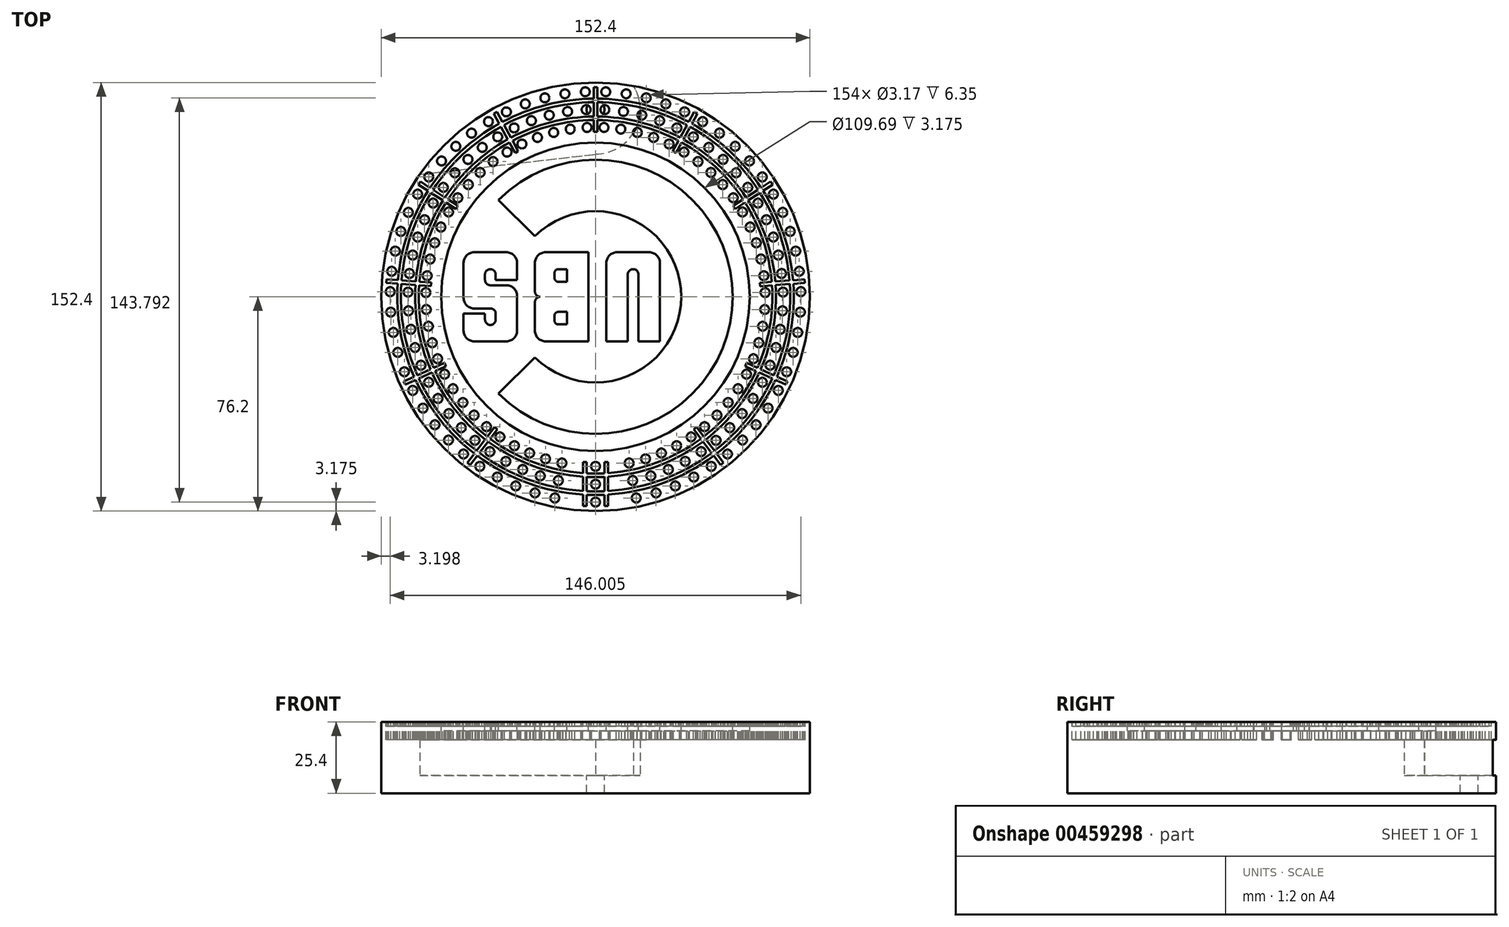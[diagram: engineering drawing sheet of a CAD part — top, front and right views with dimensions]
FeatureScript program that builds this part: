
annotation { "Feature Type Name" : "Feature", "Feature Type Description" : "" }
export const myFeature = defineFeature(function(context is Context, id is Id, definition is map)
    precondition{}
    {
        {
            var Q0;
            Q0=qCreatedBy(makeId("Top.planeOp"),FACE);
            var sketch = newSketch(context, id + "F0", { "sketchPlane" : qUnion([Q0])});
            skCircle(sketch, "E0", {"center": v(0, 0) * mm, "radius": 76.2 * mm});
            skSolve(sketch);
        }
        {
            var Q0;
            Q0=makeQuery(id+"F0.imprint","IMPRINT",FACE,{"disambiguationData":[TD([[makeQuery(id+"F0.imprint","IMPRINT",EDGE,{"derivedFrom":sQuery(id+"F0.wireOp",EDGE,"E0")}),1.0]])]});
            extrude(context, id + "F1", {"entities" : qUnion([Q0]), "depth" : 6.35 * mm});
        }
        {
            var Q0;
            Q0=makeQuery(id+"F1.opExtrude","CAP_FACE",FACE,{"disambiguationData":[OSD([sQuery(id+"F0.wireOp",EDGE,"E0")])],"isStart":false});
            var sketch = newSketch(context, id + "F2", { "sketchPlane" : qUnion([Q0])});
            skCircle(sketch, "E1", {"center": v(0, 66.68) * mm, "radius": 3.18 * mm});
            skSolve(sketch);
        }
        {
            var Q0;
            Q0 = qSketchRegion(id + "F2", true);
            extrude(context, id + "F3", {"entities" : qUnion([Q0]), "operationType" : NewBodyOperationType.REMOVE, "oppositeDirection" : true, "depth" : 6.35 * mm});
        }
        {
            var Q0;
            Q0=makeQuery(id+"F1.opExtrude","CAP_FACE",FACE,{"disambiguationData":[OSD([sQuery(id+"F0.wireOp",EDGE,"E0")])],"isStart":false});
            var sketch = newSketch(context, id + "F4", { "sketchPlane" : qUnion([Q0])});
            skArc(sketch, "E2", {"start": v(0, 50.8) * mm, "mid": v(13.86, 58.93) * mm, "end": v(13.52, 75) * mm});
            skLineSegment(sketch, "E3", {"start": v(-62.53, 43.54) * mm, "end": v(0, 50.7) * mm});
            skLineSegment(sketch, "E4", {"start": v(0, 50.7) * mm, "end": v(0, 50.8) * mm});
            skSolve(sketch);
        }
        {
            var Q0;
            {var subQ0=sQuery(id+"F4.wireOp",EDGE,"E2");Q0=makeQuery(id+"F4.imprint","IMPRINT",FACE,{"disambiguationData":[TD([[makeQuery(id+"F4.imprint","IMPRINT",EDGE,{"derivedFrom":subQ0}),-1.0]])]});}
            extrude(context, id + "F5", {"entities" : qUnion([Q0]), "operationType" : NewBodyOperationType.ADD, "depth" : 12.7 * mm});
        }
        {
            var Q0;
            Q0=makeQuery(id+"F5.opExtrude","CAP_FACE",FACE,{"disambiguationData":[OSD([sQuery(id+"F0.wireOp",EDGE,"E0"),sQuery(id+"F4.wireOp",EDGE,"E2"),sQuery(id+"F4.wireOp",EDGE,"E3"),sQuery(id+"F4.wireOp",EDGE,"E4")])],"isStart":false});
            var sketch = newSketch(context, id + "F6", { "sketchPlane" : qUnion([Q0])});
            skCircle(sketch, "E5", {"center": v(0, 0) * mm, "radius": 76.2 * mm});
            skSolve(sketch);
        }
        {
            var Q0;
            {var subQ1=makeQuery(id+"F5.opExtrude","CAP_EDGE",EDGE,{"disambiguationData":[OSD([sQuery(id+"F4.wireOp",EDGE,"E2")])],"isStart":false});Q0=makeQuery(id+"F6.imprint","IMPRINT",FACE,{"disambiguationData":[TD([[makeQuery(id+"F6.imprint","IMPRINT",EDGE,{"derivedFrom":subQ1}),-1.0]])]});}
            var Q1;
            {var subQ1=makeQuery(id+"F5.opExtrude","CAP_EDGE",EDGE,{"disambiguationData":[OSD([sQuery(id+"F4.wireOp",EDGE,"E2")])],"isStart":false});Q1=makeQuery(id+"F6.imprint","IMPRINT",FACE,{"disambiguationData":[TD([[makeQuery(id+"F6.imprint","IMPRINT",EDGE,{"derivedFrom":subQ1}),1.0]])]});}
            extrude(context, id + "F7", {"entities" : qUnion([Q0, Q1]), "operationType" : NewBodyOperationType.ADD, "depth" : 6.35 * mm});
        }
        {
            var Q0;
            Q0=makeQuery(id+"F7.opExtrude","CAP_FACE",FACE,{"disambiguationData":[OSD([sQuery(id+"F6.wireOp",EDGE,"E5")])],"isStart":false});
            var sketch = newSketch(context, id + "F8", { "sketchPlane" : qUnion([Q0])});
            skCircle(sketch, "E6", {"center": v(0, -73.03) * mm, "radius": 1.59 * mm});
            skCircle(sketch, "E7.1.0", {"center": v(7.27, -72.66) * mm, "radius": 1.59 * mm});
            skCircle(sketch, "E7.2.0", {"center": v(14.47, -71.58) * mm, "radius": 1.59 * mm});
            skCircle(sketch, "E7.3.0", {"center": v(21.52, -69.78) * mm, "radius": 1.59 * mm});
            skCircle(sketch, "E7.4.0", {"center": v(28.37, -67.3) * mm, "radius": 1.59 * mm});
            skCircle(sketch, "E7.5.0", {"center": v(34.92, -64.13) * mm, "radius": 1.59 * mm});
            skCircle(sketch, "E7.6.0", {"center": v(41.14, -60.34) * mm, "radius": 1.59 * mm});
            skCircle(sketch, "E7.7.0", {"center": v(46.94, -55.94) * mm, "radius": 1.59 * mm});
            skCircle(sketch, "E7.8.0", {"center": v(52.28, -50.99) * mm, "radius": 1.59 * mm});
            skCircle(sketch, "E7.9.0", {"center": v(57.1, -45.53) * mm, "radius": 1.59 * mm});
            skCircle(sketch, "E7.10.0", {"center": v(61.34, -39.62) * mm, "radius": 1.59 * mm});
            skCircle(sketch, "E7.11.0", {"center": v(64.98, -33.31) * mm, "radius": 1.59 * mm});
            skCircle(sketch, "E7.12.0", {"center": v(67.98, -26.68) * mm, "radius": 1.59 * mm});
            skCircle(sketch, "E7.13.0", {"center": v(70.3, -19.78) * mm, "radius": 1.59 * mm});
            skCircle(sketch, "E7.14.0", {"center": v(71.92, -12.68) * mm, "radius": 1.59 * mm});
            skCircle(sketch, "E7.15.0", {"center": v(72.82, -5.46) * mm, "radius": 1.59 * mm});
            skCircle(sketch, "E7.16.0", {"center": v(73, 1.82) * mm, "radius": 1.59 * mm});
            skCircle(sketch, "E7.17.0", {"center": v(72.46, 9.08) * mm, "radius": 1.59 * mm});
            skCircle(sketch, "E7.18.0", {"center": v(71.2, 16.25) * mm, "radius": 1.59 * mm});
            skCircle(sketch, "E7.19.0", {"center": v(69.22, 23.26) * mm, "radius": 1.59 * mm});
            skCircle(sketch, "E7.20.0", {"center": v(66.56, 30.03) * mm, "radius": 1.59 * mm});
            skCircle(sketch, "E7.21.0", {"center": v(63.24, 36.51) * mm, "radius": 1.59 * mm});
            skCircle(sketch, "E7.22.0", {"center": v(59.3, 42.63) * mm, "radius": 1.59 * mm});
            skCircle(sketch, "E7.23.0", {"center": v(54.75, 48.32) * mm, "radius": 1.59 * mm});
            skCircle(sketch, "E7.24.0", {"center": v(49.67, 53.53) * mm, "radius": 1.59 * mm});
            skCircle(sketch, "E7.25.0", {"center": v(44.1, 58.21) * mm, "radius": 1.59 * mm});
            skCircle(sketch, "E7.26.0", {"center": v(38.08, 62.31) * mm, "radius": 1.59 * mm});
            skCircle(sketch, "E7.27.0", {"center": v(31.68, 65.8) * mm, "radius": 1.59 * mm});
            skCircle(sketch, "E7.28.0", {"center": v(24.98, 68.62) * mm, "radius": 1.59 * mm});
            skCircle(sketch, "E7.29.0", {"center": v(18.02, 70.77) * mm, "radius": 1.59 * mm});
            skCircle(sketch, "E7.30.0", {"center": v(10.88, 72.2) * mm, "radius": 1.59 * mm});
            skCircle(sketch, "E7.31.0", {"center": v(3.64, 72.93) * mm, "radius": 1.59 * mm});
            skCircle(sketch, "E7.32.0", {"center": v(-3.64, 72.93) * mm, "radius": 1.59 * mm});
            skCircle(sketch, "E7.33.0", {"center": v(-10.88, 72.2) * mm, "radius": 1.59 * mm});
            skCircle(sketch, "E7.34.0", {"center": v(-18.02, 70.77) * mm, "radius": 1.59 * mm});
            skCircle(sketch, "E7.35.0", {"center": v(-24.98, 68.62) * mm, "radius": 1.59 * mm});
            skCircle(sketch, "E7.36.0", {"center": v(-31.68, 65.8) * mm, "radius": 1.59 * mm});
            skCircle(sketch, "E7.37.0", {"center": v(-38.08, 62.31) * mm, "radius": 1.59 * mm});
            skCircle(sketch, "E7.38.0", {"center": v(-44.1, 58.21) * mm, "radius": 1.59 * mm});
            skCircle(sketch, "E7.39.0", {"center": v(-49.67, 53.53) * mm, "radius": 1.59 * mm});
            skCircle(sketch, "E7.40.0", {"center": v(-54.75, 48.32) * mm, "radius": 1.59 * mm});
            skCircle(sketch, "E7.41.0", {"center": v(-59.3, 42.63) * mm, "radius": 1.59 * mm});
            skCircle(sketch, "E7.42.0", {"center": v(-63.24, 36.51) * mm, "radius": 1.59 * mm});
            skCircle(sketch, "E7.43.0", {"center": v(-66.56, 30.03) * mm, "radius": 1.59 * mm});
            skCircle(sketch, "E7.44.0", {"center": v(-69.22, 23.26) * mm, "radius": 1.59 * mm});
            skCircle(sketch, "E7.45.0", {"center": v(-71.2, 16.25) * mm, "radius": 1.59 * mm});
            skCircle(sketch, "E7.46.0", {"center": v(-72.46, 9.08) * mm, "radius": 1.59 * mm});
            skCircle(sketch, "E7.47.0", {"center": v(-73, 1.82) * mm, "radius": 1.59 * mm});
            skCircle(sketch, "E7.48.0", {"center": v(-72.82, -5.46) * mm, "radius": 1.59 * mm});
            skCircle(sketch, "E7.49.0", {"center": v(-71.92, -12.68) * mm, "radius": 1.59 * mm});
            skCircle(sketch, "E7.50.0", {"center": v(-70.3, -19.78) * mm, "radius": 1.59 * mm});
            skCircle(sketch, "E7.51.0", {"center": v(-67.98, -26.68) * mm, "radius": 1.59 * mm});
            skCircle(sketch, "E7.52.0", {"center": v(-64.98, -33.31) * mm, "radius": 1.59 * mm});
            skCircle(sketch, "E7.53.0", {"center": v(-61.34, -39.62) * mm, "radius": 1.59 * mm});
            skCircle(sketch, "E7.54.0", {"center": v(-57.1, -45.53) * mm, "radius": 1.59 * mm});
            skCircle(sketch, "E7.55.0", {"center": v(-52.28, -50.99) * mm, "radius": 1.59 * mm});
            skCircle(sketch, "E7.56.0", {"center": v(-46.94, -55.94) * mm, "radius": 1.59 * mm});
            skCircle(sketch, "E7.57.0", {"center": v(-41.14, -60.34) * mm, "radius": 1.59 * mm});
            skCircle(sketch, "E7.58.0", {"center": v(-34.92, -64.13) * mm, "radius": 1.59 * mm});
            skCircle(sketch, "E7.59.0", {"center": v(-28.37, -67.3) * mm, "radius": 1.59 * mm});
            skCircle(sketch, "E7.60.0", {"center": v(-21.52, -69.78) * mm, "radius": 1.59 * mm});
            skCircle(sketch, "E7.61.0", {"center": v(-14.47, -71.58) * mm, "radius": 1.59 * mm});
            skCircle(sketch, "E7.62.0", {"center": v(-7.27, -72.66) * mm, "radius": 1.59 * mm});
            skPoint(sketch, "E7.center", {"position": v(0, 0) * mm});
            skSolve(sketch);
        }
        {
            var Q0;
            Q0=makeQuery(id+"F8.imprint","IMPRINT",FACE,{"disambiguationData":[TD([[makeQuery(id+"F8.imprint","IMPRINT",EDGE,{"derivedFrom":sQuery(id+"F8.wireOp",EDGE,"E6")}),-1.0]])]});
            var sketch = newSketch(context, id + "F9", { "sketchPlane" : qUnion([Q0])});
            skCircle(sketch, "E8", {"center": v(0, -66.67) * mm, "radius": 1.59 * mm});
            skCircle(sketch, "E9.1.0", {"center": v(6.64, -66.34) * mm, "radius": 1.59 * mm});
            skCircle(sketch, "E9.2.0", {"center": v(13.21, -65.35) * mm, "radius": 1.59 * mm});
            skCircle(sketch, "E9.3.0", {"center": v(19.65, -63.71) * mm, "radius": 1.59 * mm});
            skCircle(sketch, "E9.4.0", {"center": v(25.9, -61.44) * mm, "radius": 1.59 * mm});
            skCircle(sketch, "E9.5.0", {"center": v(31.89, -58.56) * mm, "radius": 1.59 * mm});
            skCircle(sketch, "E9.6.0", {"center": v(37.56, -55.09) * mm, "radius": 1.59 * mm});
            skCircle(sketch, "E9.7.0", {"center": v(42.86, -51.08) * mm, "radius": 1.59 * mm});
            skCircle(sketch, "E9.8.0", {"center": v(47.73, -46.55) * mm, "radius": 1.59 * mm});
            skCircle(sketch, "E9.9.0", {"center": v(52.13, -41.57) * mm, "radius": 1.59 * mm});
            skCircle(sketch, "E9.10.0", {"center": v(56, -36.17) * mm, "radius": 1.59 * mm});
            skCircle(sketch, "E9.11.0", {"center": v(59.33, -30.42) * mm, "radius": 1.59 * mm});
            skCircle(sketch, "E9.12.0", {"center": v(62.07, -24.36) * mm, "radius": 1.59 * mm});
            skCircle(sketch, "E9.13.0", {"center": v(64.18, -18.06) * mm, "radius": 1.59 * mm});
            skCircle(sketch, "E9.14.0", {"center": v(65.66, -11.58) * mm, "radius": 1.59 * mm});
            skCircle(sketch, "E9.15.0", {"center": v(66.49, -4.98) * mm, "radius": 1.59 * mm});
            skCircle(sketch, "E9.16.0", {"center": v(66.65, 1.66) * mm, "radius": 1.59 * mm});
            skCircle(sketch, "E9.17.0", {"center": v(66.16, 8.3) * mm, "radius": 1.59 * mm});
            skCircle(sketch, "E9.18.0", {"center": v(65, 14.84) * mm, "radius": 1.59 * mm});
            skCircle(sketch, "E9.19.0", {"center": v(63.2, 21.24) * mm, "radius": 1.59 * mm});
            skCircle(sketch, "E9.20.0", {"center": v(60.77, 27.42) * mm, "radius": 1.59 * mm});
            skCircle(sketch, "E9.21.0", {"center": v(57.74, 33.34) * mm, "radius": 1.59 * mm});
            skCircle(sketch, "E9.22.0", {"center": v(54.14, 38.92) * mm, "radius": 1.59 * mm});
            skCircle(sketch, "E9.23.0", {"center": v(50, 44.12) * mm, "radius": 1.59 * mm});
            skCircle(sketch, "E9.24.0", {"center": v(45.35, 48.88) * mm, "radius": 1.59 * mm});
            skCircle(sketch, "E9.25.0", {"center": v(40.26, 53.15) * mm, "radius": 1.59 * mm});
            skCircle(sketch, "E9.26.0", {"center": v(34.77, 56.9) * mm, "radius": 1.59 * mm});
            skCircle(sketch, "E9.27.0", {"center": v(28.93, 60.07) * mm, "radius": 1.59 * mm});
            skCircle(sketch, "E9.28.0", {"center": v(22.8, 62.65) * mm, "radius": 1.59 * mm});
            skCircle(sketch, "E9.29.0", {"center": v(16.45, 64.61) * mm, "radius": 1.59 * mm});
            skCircle(sketch, "E9.30.0", {"center": v(9.94, 65.93) * mm, "radius": 1.59 * mm});
            skCircle(sketch, "E9.31.0", {"center": v(3.32, 66.6) * mm, "radius": 1.59 * mm});
            skCircle(sketch, "E9.32.0", {"center": v(-3.32, 66.6) * mm, "radius": 1.59 * mm});
            skCircle(sketch, "E9.33.0", {"center": v(-9.94, 65.93) * mm, "radius": 1.59 * mm});
            skCircle(sketch, "E9.34.0", {"center": v(-16.45, 64.61) * mm, "radius": 1.59 * mm});
            skCircle(sketch, "E9.35.0", {"center": v(-22.8, 62.65) * mm, "radius": 1.59 * mm});
            skCircle(sketch, "E9.36.0", {"center": v(-28.93, 60.07) * mm, "radius": 1.59 * mm});
            skCircle(sketch, "E9.37.0", {"center": v(-34.77, 56.9) * mm, "radius": 1.59 * mm});
            skCircle(sketch, "E9.38.0", {"center": v(-40.26, 53.15) * mm, "radius": 1.59 * mm});
            skCircle(sketch, "E9.39.0", {"center": v(-45.35, 48.88) * mm, "radius": 1.59 * mm});
            skCircle(sketch, "E9.40.0", {"center": v(-50, 44.12) * mm, "radius": 1.59 * mm});
            skCircle(sketch, "E9.41.0", {"center": v(-54.14, 38.92) * mm, "radius": 1.59 * mm});
            skCircle(sketch, "E9.42.0", {"center": v(-57.74, 33.34) * mm, "radius": 1.59 * mm});
            skCircle(sketch, "E9.43.0", {"center": v(-60.77, 27.42) * mm, "radius": 1.59 * mm});
            skCircle(sketch, "E9.44.0", {"center": v(-63.2, 21.24) * mm, "radius": 1.59 * mm});
            skCircle(sketch, "E9.45.0", {"center": v(-65, 14.84) * mm, "radius": 1.59 * mm});
            skCircle(sketch, "E9.46.0", {"center": v(-66.16, 8.3) * mm, "radius": 1.59 * mm});
            skCircle(sketch, "E9.47.0", {"center": v(-66.65, 1.66) * mm, "radius": 1.59 * mm});
            skCircle(sketch, "E9.48.0", {"center": v(-66.49, -4.98) * mm, "radius": 1.59 * mm});
            skCircle(sketch, "E9.49.0", {"center": v(-65.66, -11.58) * mm, "radius": 1.59 * mm});
            skCircle(sketch, "E9.50.0", {"center": v(-64.18, -18.06) * mm, "radius": 1.59 * mm});
            skCircle(sketch, "E9.51.0", {"center": v(-62.07, -24.36) * mm, "radius": 1.59 * mm});
            skCircle(sketch, "E9.52.0", {"center": v(-59.33, -30.42) * mm, "radius": 1.59 * mm});
            skCircle(sketch, "E9.53.0", {"center": v(-56, -36.17) * mm, "radius": 1.59 * mm});
            skCircle(sketch, "E9.54.0", {"center": v(-52.13, -41.57) * mm, "radius": 1.59 * mm});
            skCircle(sketch, "E9.55.0", {"center": v(-47.73, -46.55) * mm, "radius": 1.59 * mm});
            skCircle(sketch, "E9.56.0", {"center": v(-42.86, -51.08) * mm, "radius": 1.59 * mm});
            skCircle(sketch, "E9.57.0", {"center": v(-37.56, -55.09) * mm, "radius": 1.59 * mm});
            skCircle(sketch, "E9.58.0", {"center": v(-31.89, -58.56) * mm, "radius": 1.59 * mm});
            skCircle(sketch, "E9.59.0", {"center": v(-25.9, -61.44) * mm, "radius": 1.59 * mm});
            skCircle(sketch, "E9.60.0", {"center": v(-19.65, -63.71) * mm, "radius": 1.59 * mm});
            skCircle(sketch, "E9.61.0", {"center": v(-13.21, -65.35) * mm, "radius": 1.59 * mm});
            skCircle(sketch, "E9.62.0", {"center": v(-6.64, -66.34) * mm, "radius": 1.59 * mm});
            skPoint(sketch, "E9.center", {"position": v(0, 0) * mm});
            skSolve(sketch);
        }
        {
            var Q0;
            Q0=makeQuery(id+"F8.imprint","IMPRINT",FACE,{"disambiguationData":[TD([[makeQuery(id+"F8.imprint","IMPRINT",EDGE,{"derivedFrom":sQuery(id+"F8.wireOp",EDGE,"E6")}),-1.0]])]});
            var sketch = newSketch(context, id + "F10", { "sketchPlane" : qUnion([Q0])});
            skCircle(sketch, "E10", {"center": v(0, -60.33) * mm, "radius": 1.59 * mm});
            skCircle(sketch, "E11.1.0", {"center": v(6, -60.03) * mm, "radius": 1.59 * mm});
            skCircle(sketch, "E11.2.0", {"center": v(11.95, -59.13) * mm, "radius": 1.59 * mm});
            skCircle(sketch, "E11.3.0", {"center": v(17.78, -57.64) * mm, "radius": 1.59 * mm});
            skCircle(sketch, "E11.4.0", {"center": v(23.43, -55.59) * mm, "radius": 1.59 * mm});
            skCircle(sketch, "E11.5.0", {"center": v(28.85, -52.98) * mm, "radius": 1.59 * mm});
            skCircle(sketch, "E11.6.0", {"center": v(33.98, -49.84) * mm, "radius": 1.59 * mm});
            skCircle(sketch, "E11.7.0", {"center": v(38.78, -46.21) * mm, "radius": 1.59 * mm});
            skCircle(sketch, "E11.8.0", {"center": v(43.18, -42.12) * mm, "radius": 1.59 * mm});
            skCircle(sketch, "E11.9.0", {"center": v(47.16, -37.61) * mm, "radius": 1.59 * mm});
            skCircle(sketch, "E11.10.0", {"center": v(50.67, -32.73) * mm, "radius": 1.59 * mm});
            skCircle(sketch, "E11.11.0", {"center": v(53.68, -27.52) * mm, "radius": 1.59 * mm});
            skCircle(sketch, "E11.12.0", {"center": v(56.15, -22.04) * mm, "radius": 1.59 * mm});
            skCircle(sketch, "E11.13.0", {"center": v(58.07, -16.34) * mm, "radius": 1.59 * mm});
            skCircle(sketch, "E11.14.0", {"center": v(59.4, -10.48) * mm, "radius": 1.59 * mm});
            skCircle(sketch, "E11.15.0", {"center": v(60.16, -4.5) * mm, "radius": 1.59 * mm});
            skCircle(sketch, "E11.16.0", {"center": v(60.3, 1.5) * mm, "radius": 1.59 * mm});
            skCircle(sketch, "E11.17.0", {"center": v(59.86, 7.5) * mm, "radius": 1.59 * mm});
            skCircle(sketch, "E11.18.0", {"center": v(58.81, 13.42) * mm, "radius": 1.59 * mm});
            skCircle(sketch, "E11.19.0", {"center": v(57.18, 19.21) * mm, "radius": 1.59 * mm});
            skCircle(sketch, "E11.20.0", {"center": v(54.99, 24.81) * mm, "radius": 1.59 * mm});
            skCircle(sketch, "E11.21.0", {"center": v(52.24, 30.16) * mm, "radius": 1.59 * mm});
            skCircle(sketch, "E11.22.0", {"center": v(48.98, 35.21) * mm, "radius": 1.59 * mm});
            skCircle(sketch, "E11.23.0", {"center": v(45.23, 39.92) * mm, "radius": 1.59 * mm});
            skCircle(sketch, "E11.24.0", {"center": v(41.03, 44.22) * mm, "radius": 1.59 * mm});
            skCircle(sketch, "E11.25.0", {"center": v(36.42, 48.09) * mm, "radius": 1.59 * mm});
            skCircle(sketch, "E11.26.0", {"center": v(31.46, 51.47) * mm, "radius": 1.59 * mm});
            skCircle(sketch, "E11.27.0", {"center": v(26.17, 54.35) * mm, "radius": 1.59 * mm});
            skCircle(sketch, "E11.28.0", {"center": v(20.63, 56.69) * mm, "radius": 1.59 * mm});
            skCircle(sketch, "E11.29.0", {"center": v(14.89, 58.46) * mm, "radius": 1.59 * mm});
            skCircle(sketch, "E11.30.0", {"center": v(9, 59.65) * mm, "radius": 1.59 * mm});
            skCircle(sketch, "E11.31.0", {"center": v(3, 60.25) * mm, "radius": 1.59 * mm});
            skCircle(sketch, "E11.32.0", {"center": v(-3, 60.25) * mm, "radius": 1.59 * mm});
            skCircle(sketch, "E11.33.0", {"center": v(-9, 59.65) * mm, "radius": 1.59 * mm});
            skCircle(sketch, "E11.34.0", {"center": v(-14.89, 58.46) * mm, "radius": 1.59 * mm});
            skCircle(sketch, "E11.35.0", {"center": v(-20.63, 56.69) * mm, "radius": 1.59 * mm});
            skCircle(sketch, "E11.36.0", {"center": v(-26.17, 54.35) * mm, "radius": 1.59 * mm});
            skCircle(sketch, "E11.37.0", {"center": v(-31.46, 51.47) * mm, "radius": 1.59 * mm});
            skCircle(sketch, "E11.38.0", {"center": v(-36.42, 48.09) * mm, "radius": 1.59 * mm});
            skCircle(sketch, "E11.39.0", {"center": v(-41.03, 44.22) * mm, "radius": 1.59 * mm});
            skCircle(sketch, "E11.40.0", {"center": v(-45.23, 39.92) * mm, "radius": 1.59 * mm});
            skCircle(sketch, "E11.41.0", {"center": v(-48.98, 35.21) * mm, "radius": 1.59 * mm});
            skCircle(sketch, "E11.42.0", {"center": v(-52.24, 30.16) * mm, "radius": 1.59 * mm});
            skCircle(sketch, "E11.43.0", {"center": v(-54.99, 24.81) * mm, "radius": 1.59 * mm});
            skCircle(sketch, "E11.44.0", {"center": v(-57.18, 19.21) * mm, "radius": 1.59 * mm});
            skCircle(sketch, "E11.45.0", {"center": v(-58.81, 13.42) * mm, "radius": 1.59 * mm});
            skCircle(sketch, "E11.46.0", {"center": v(-59.86, 7.5) * mm, "radius": 1.59 * mm});
            skCircle(sketch, "E11.47.0", {"center": v(-60.3, 1.5) * mm, "radius": 1.59 * mm});
            skCircle(sketch, "E11.48.0", {"center": v(-60.16, -4.5) * mm, "radius": 1.59 * mm});
            skCircle(sketch, "E11.49.0", {"center": v(-59.4, -10.48) * mm, "radius": 1.59 * mm});
            skCircle(sketch, "E11.50.0", {"center": v(-58.07, -16.34) * mm, "radius": 1.59 * mm});
            skCircle(sketch, "E11.51.0", {"center": v(-56.15, -22.04) * mm, "radius": 1.59 * mm});
            skCircle(sketch, "E11.52.0", {"center": v(-53.68, -27.52) * mm, "radius": 1.59 * mm});
            skCircle(sketch, "E11.53.0", {"center": v(-50.67, -32.73) * mm, "radius": 1.59 * mm});
            skCircle(sketch, "E11.54.0", {"center": v(-47.16, -37.61) * mm, "radius": 1.59 * mm});
            skCircle(sketch, "E11.55.0", {"center": v(-43.18, -42.12) * mm, "radius": 1.59 * mm});
            skCircle(sketch, "E11.56.0", {"center": v(-38.78, -46.21) * mm, "radius": 1.59 * mm});
            skCircle(sketch, "E11.57.0", {"center": v(-33.98, -49.84) * mm, "radius": 1.59 * mm});
            skCircle(sketch, "E11.58.0", {"center": v(-28.85, -52.98) * mm, "radius": 1.59 * mm});
            skCircle(sketch, "E11.59.0", {"center": v(-23.43, -55.59) * mm, "radius": 1.59 * mm});
            skCircle(sketch, "E11.60.0", {"center": v(-17.78, -57.64) * mm, "radius": 1.59 * mm});
            skCircle(sketch, "E11.61.0", {"center": v(-11.95, -59.13) * mm, "radius": 1.59 * mm});
            skCircle(sketch, "E11.62.0", {"center": v(-6, -60.03) * mm, "radius": 1.59 * mm});
            skPoint(sketch, "E11.center", {"position": v(0, 0) * mm});
            skSolve(sketch);
        }
        {
            var Q0;
            Q0 = qSketchRegion(id + "F8", true);
            extrude(context, id + "F11", {"entities" : qUnion([Q0]), "operationType" : NewBodyOperationType.REMOVE, "oppositeDirection" : true, "depth" : 6.35 * mm});
        }
        {
            var Q0;
            Q0 = qSketchRegion(id + "F9", true);
            extrude(context, id + "F12", {"entities" : qUnion([Q0]), "operationType" : NewBodyOperationType.REMOVE, "oppositeDirection" : true, "depth" : 6.35 * mm});
        }
        {
            var Q0;
            Q0 = qSketchRegion(id + "F10", true);
            extrude(context, id + "F13", {"entities" : qUnion([Q0]), "operationType" : NewBodyOperationType.REMOVE, "oppositeDirection" : true, "depth" : 6.35 * mm});
        }
        {
            var Q0;
            Q0=makeQuery(id+"F13.boolean.opBoolean","COPY",FACE,{"derivedFrom":makeQuery(id+"F13.opExtrude","CAP_FACE",FACE,{"disambiguationData":[OSD([sQuery(id+"F10.wireOp",EDGE,"E11.1.0")])],"isStart":false})});
            extrude(context, id + "F14", {"entities" : qUnion([Q0]), "operationType" : NewBodyOperationType.ADD, "depth" : 6.35 * mm});
        }
        {
            var Q0;
            Q0=makeQuery(id+"F12.boolean.opBoolean","COPY",FACE,{"derivedFrom":makeQuery(id+"F12.opExtrude","CAP_FACE",FACE,{"disambiguationData":[OSD([sQuery(id+"F9.wireOp",EDGE,"E9.1.0")])],"isStart":false})});
            extrude(context, id + "F15", {"entities" : qUnion([Q0]), "operationType" : NewBodyOperationType.ADD, "depth" : 6.35 * mm});
        }
        {
            var Q0;
            Q0=makeQuery(id+"F11.boolean.opBoolean","COPY",FACE,{"derivedFrom":makeQuery(id+"F11.opExtrude","CAP_FACE",FACE,{"disambiguationData":[OSD([sQuery(id+"F8.wireOp",EDGE,"E7.1.0")])],"isStart":false})});
            extrude(context, id + "F16", {"entities" : qUnion([Q0]), "operationType" : NewBodyOperationType.ADD, "depth" : 6.35 * mm});
        }
        {
            var Q0;
            Q0=makeQuery(id+"F13.boolean.opBoolean","COPY",FACE,{"derivedFrom":makeQuery(id+"F13.opExtrude","CAP_FACE",FACE,{"disambiguationData":[OSD([sQuery(id+"F10.wireOp",EDGE,"E11.62.0")])],"isStart":false})});
            extrude(context, id + "F17", {"entities" : qUnion([Q0]), "operationType" : NewBodyOperationType.ADD, "depth" : 6.35 * mm});
        }
        {
            var Q0;
            Q0=makeQuery(id+"F12.boolean.opBoolean","COPY",FACE,{"derivedFrom":makeQuery(id+"F12.opExtrude","CAP_FACE",FACE,{"disambiguationData":[OSD([sQuery(id+"F9.wireOp",EDGE,"E9.62.0")])],"isStart":false})});
            extrude(context, id + "F18", {"entities" : qUnion([Q0]), "operationType" : NewBodyOperationType.ADD, "depth" : 6.35 * mm});
        }
        {
            var Q0;
            Q0=makeQuery(id+"F11.boolean.opBoolean","COPY",FACE,{"derivedFrom":makeQuery(id+"F11.opExtrude","CAP_FACE",FACE,{"disambiguationData":[OSD([sQuery(id+"F8.wireOp",EDGE,"E7.62.0")])],"isStart":false})});
            extrude(context, id + "F19", {"entities" : qUnion([Q0]), "operationType" : NewBodyOperationType.ADD, "depth" : 6.35 * mm});
        }
        {
            var Q0;
            Q0=makeQuery(id+"F19.boolean.opBoolean","MERGE",FACE,{"derivedFrom":[makeQuery(id+"F18.boolean.opBoolean","MERGE",FACE,{"derivedFrom":[makeQuery(id+"F17.boolean.opBoolean","MERGE",FACE,{"derivedFrom":[makeQuery(id+"F16.boolean.opBoolean","MERGE",FACE,{"derivedFrom":[makeQuery(id+"F15.boolean.opBoolean","MERGE",FACE,{"derivedFrom":[makeQuery(id+"F14.boolean.opBoolean","MERGE",FACE,{"derivedFrom":[makeQuery(id+"F7.opExtrude","CAP_FACE",FACE,{"disambiguationData":[OSD([sQuery(id+"F6.wireOp",EDGE,"E5")])],"isStart":false}),makeQuery(id+"F14.opExtrude","CAP_FACE",FACE,{"disambiguationData":[OSD([sQuery(id+"F10.wireOp",EDGE,"E11.1.0")])],"isStart":false})]}),makeQuery(id+"F15.opExtrude","CAP_FACE",FACE,{"disambiguationData":[OSD([sQuery(id+"F9.wireOp",EDGE,"E9.1.0")])],"isStart":false})]}),makeQuery(id+"F16.opExtrude","CAP_FACE",FACE,{"disambiguationData":[OSD([sQuery(id+"F8.wireOp",EDGE,"E7.1.0")])],"isStart":false})]}),makeQuery(id+"F17.opExtrude","CAP_FACE",FACE,{"disambiguationData":[OSD([sQuery(id+"F10.wireOp",EDGE,"E11.62.0")])],"isStart":false})]}),makeQuery(id+"F18.opExtrude","CAP_FACE",FACE,{"disambiguationData":[OSD([sQuery(id+"F9.wireOp",EDGE,"E9.62.0")])],"isStart":false})]}),makeQuery(id+"F19.opExtrude","CAP_FACE",FACE,{"disambiguationData":[OSD([sQuery(id+"F8.wireOp",EDGE,"E7.62.0")])],"isStart":false})]});
            var sketch = newSketch(context, id + "F20", { "sketchPlane" : qUnion([Q0])});
            skCircle(sketch, "E12", {"center": v(0, 0) * mm, "radius": 62.87 * mm});
            skCircle(sketch, "E13", {"center": v(0, 0) * mm, "radius": 64.13 * mm});
            skSolve(sketch);
        }
        {
            var Q0;
            Q0=makeQuery(id+"F20.imprint","IMPRINT",FACE,{"disambiguationData":[TD([[makeQuery(id+"F20.imprint","IMPRINT",EDGE,{"derivedFrom":sQuery(id+"F20.wireOp",EDGE,"E12")}),-1.0]])]});
            extrude(context, id + "F21", {"entities" : qUnion([Q0]), "operationType" : NewBodyOperationType.REMOVE, "oppositeDirection" : true, "depth" : 1.59 * mm});
        }
        {
            var Q0;
            Q0=makeQuery(id+"F21.boolean.opBoolean","SPLIT",FACE,{"disambiguationData":[TD([makeQuery(id+"F13.boolean.opBoolean","COPY",FACE,{"derivedFrom":makeQuery(id+"F13.opExtrude","SWEPT_FACE",FACE,{"disambiguationData":[OSD([sQuery(id+"F10.wireOp",EDGE,"E10")])]})})])],"derivedFrom":makeQuery(id+"F19.boolean.opBoolean","MERGE",FACE,{"derivedFrom":[makeQuery(id+"F18.boolean.opBoolean","MERGE",FACE,{"derivedFrom":[makeQuery(id+"F17.boolean.opBoolean","MERGE",FACE,{"derivedFrom":[makeQuery(id+"F16.boolean.opBoolean","MERGE",FACE,{"derivedFrom":[makeQuery(id+"F15.boolean.opBoolean","MERGE",FACE,{"derivedFrom":[makeQuery(id+"F14.boolean.opBoolean","MERGE",FACE,{"derivedFrom":[makeQuery(id+"F7.opExtrude","CAP_FACE",FACE,{"disambiguationData":[OSD([sQuery(id+"F6.wireOp",EDGE,"E5")])],"isStart":false}),makeQuery(id+"F14.opExtrude","CAP_FACE",FACE,{"disambiguationData":[OSD([sQuery(id+"F10.wireOp",EDGE,"E11.1.0")])],"isStart":false})]}),makeQuery(id+"F15.opExtrude","CAP_FACE",FACE,{"disambiguationData":[OSD([sQuery(id+"F9.wireOp",EDGE,"E9.1.0")])],"isStart":false})]}),makeQuery(id+"F16.opExtrude","CAP_FACE",FACE,{"disambiguationData":[OSD([sQuery(id+"F8.wireOp",EDGE,"E7.1.0")])],"isStart":false})]}),makeQuery(id+"F17.opExtrude","CAP_FACE",FACE,{"disambiguationData":[OSD([sQuery(id+"F10.wireOp",EDGE,"E11.62.0")])],"isStart":false})]}),makeQuery(id+"F18.opExtrude","CAP_FACE",FACE,{"disambiguationData":[OSD([sQuery(id+"F9.wireOp",EDGE,"E9.62.0")])],"isStart":false})]}),makeQuery(id+"F19.opExtrude","CAP_FACE",FACE,{"disambiguationData":[OSD([sQuery(id+"F8.wireOp",EDGE,"E7.62.0")])],"isStart":false})]})});
            var sketch = newSketch(context, id + "F22", { "sketchPlane" : qUnion([Q0])});
            skCircle(sketch, "E14", {"center": v(0, 0) * mm, "radius": 70.48 * mm});
            skCircle(sketch, "E15", {"center": v(0, 0) * mm, "radius": 69.22 * mm});
            skSolve(sketch);
        }
        {
            var Q0;
            Q0=makeQuery(id+"F22.imprint","IMPRINT",FACE,{"disambiguationData":[TD([[makeQuery(id+"F22.imprint","IMPRINT",EDGE,{"derivedFrom":sQuery(id+"F22.wireOp",EDGE,"E14")}),1.0]])]});
            extrude(context, id + "F23", {"entities" : qUnion([Q0]), "operationType" : NewBodyOperationType.REMOVE, "oppositeDirection" : true, "depth" : 1.59 * mm});
        }
        {
            var Q0;
            Q0=makeQuery(id+"F21.boolean.opBoolean","SPLIT",FACE,{"disambiguationData":[TD([makeQuery(id+"F13.boolean.opBoolean","COPY",FACE,{"derivedFrom":makeQuery(id+"F13.opExtrude","SWEPT_FACE",FACE,{"disambiguationData":[OSD([sQuery(id+"F10.wireOp",EDGE,"E10")])]})})])],"derivedFrom":makeQuery(id+"F19.boolean.opBoolean","MERGE",FACE,{"derivedFrom":[makeQuery(id+"F18.boolean.opBoolean","MERGE",FACE,{"derivedFrom":[makeQuery(id+"F17.boolean.opBoolean","MERGE",FACE,{"derivedFrom":[makeQuery(id+"F16.boolean.opBoolean","MERGE",FACE,{"derivedFrom":[makeQuery(id+"F15.boolean.opBoolean","MERGE",FACE,{"derivedFrom":[makeQuery(id+"F14.boolean.opBoolean","MERGE",FACE,{"derivedFrom":[makeQuery(id+"F7.opExtrude","CAP_FACE",FACE,{"disambiguationData":[OSD([sQuery(id+"F6.wireOp",EDGE,"E5")])],"isStart":false}),makeQuery(id+"F14.opExtrude","CAP_FACE",FACE,{"disambiguationData":[OSD([sQuery(id+"F10.wireOp",EDGE,"E11.1.0")])],"isStart":false})]}),makeQuery(id+"F15.opExtrude","CAP_FACE",FACE,{"disambiguationData":[OSD([sQuery(id+"F9.wireOp",EDGE,"E9.1.0")])],"isStart":false})]}),makeQuery(id+"F16.opExtrude","CAP_FACE",FACE,{"disambiguationData":[OSD([sQuery(id+"F8.wireOp",EDGE,"E7.1.0")])],"isStart":false})]}),makeQuery(id+"F17.opExtrude","CAP_FACE",FACE,{"disambiguationData":[OSD([sQuery(id+"F10.wireOp",EDGE,"E11.62.0")])],"isStart":false})]}),makeQuery(id+"F18.opExtrude","CAP_FACE",FACE,{"disambiguationData":[OSD([sQuery(id+"F9.wireOp",EDGE,"E9.62.0")])],"isStart":false})]}),makeQuery(id+"F19.opExtrude","CAP_FACE",FACE,{"disambiguationData":[OSD([sQuery(id+"F8.wireOp",EDGE,"E7.62.0")])],"isStart":false})]})});
            var sketch = newSketch(context, id + "F24", { "sketchPlane" : qUnion([Q0])});
            skPoint(sketch, "E16.start.orphan", {"position": v(0, -60.33) * mm});
            skPoint(sketch, "E17.start.orphan", {"position": v(0, -72.87) * mm});
            skLineSegment(sketch, "E18", {"start": v(3.18, -58.74) * mm, "end": v(3.18, -74.45) * mm});
            skLineSegment(sketch, "E19", {"start": v(4.44, -74.45) * mm, "end": v(4.44, -58.74) * mm});
            skLineSegment(sketch, "E20", {"start": v(4.44, -58.74) * mm, "end": v(3.18, -58.74) * mm});
            skLineSegment(sketch, "E21", {"start": v(4.44, -74.45) * mm, "end": v(3.18, -74.45) * mm});
            skLineSegment(sketch, "E22", {"start": v(-3.17, -58.74) * mm, "end": v(-3.18, -74.45) * mm});
            skLineSegment(sketch, "E23", {"start": v(-4.45, -58.74) * mm, "end": v(-3.17, -58.74) * mm});
            skLineSegment(sketch, "E24", {"start": v(-3.18, -74.45) * mm, "end": v(-4.45, -74.45) * mm});
            skPoint(sketch, "E25.orphan", {"position": v(-6.17, -58.74) * mm});
            skLineSegment(sketch, "E26", {"start": v(-4.45, -74.45) * mm, "end": v(-4.45, -58.74) * mm});
            skSolve(sketch);
        }
        {
            var Q0;
            Q0 = qSketchRegion(id + "F24", true);
            extrude(context, id + "F25", {"entities" : qUnion([Q0]), "operationType" : NewBodyOperationType.REMOVE, "oppositeDirection" : true, "depth" : 1.59 * mm});
        }
        {
            var Q0;
            Q0=makeQuery(id+"F21.boolean.opBoolean","SPLIT",FACE,{"disambiguationData":[TD([makeQuery(id+"F13.boolean.opBoolean","COPY",FACE,{"derivedFrom":makeQuery(id+"F13.opExtrude","SWEPT_FACE",FACE,{"disambiguationData":[OSD([sQuery(id+"F10.wireOp",EDGE,"E10")])]})})])],"derivedFrom":makeQuery(id+"F19.boolean.opBoolean","MERGE",FACE,{"derivedFrom":[makeQuery(id+"F18.boolean.opBoolean","MERGE",FACE,{"derivedFrom":[makeQuery(id+"F17.boolean.opBoolean","MERGE",FACE,{"derivedFrom":[makeQuery(id+"F16.boolean.opBoolean","MERGE",FACE,{"derivedFrom":[makeQuery(id+"F15.boolean.opBoolean","MERGE",FACE,{"derivedFrom":[makeQuery(id+"F14.boolean.opBoolean","MERGE",FACE,{"derivedFrom":[makeQuery(id+"F7.opExtrude","CAP_FACE",FACE,{"disambiguationData":[OSD([sQuery(id+"F6.wireOp",EDGE,"E5")])],"isStart":false}),makeQuery(id+"F14.opExtrude","CAP_FACE",FACE,{"disambiguationData":[OSD([sQuery(id+"F10.wireOp",EDGE,"E11.1.0")])],"isStart":false})]}),makeQuery(id+"F15.opExtrude","CAP_FACE",FACE,{"disambiguationData":[OSD([sQuery(id+"F9.wireOp",EDGE,"E9.1.0")])],"isStart":false})]}),makeQuery(id+"F16.opExtrude","CAP_FACE",FACE,{"disambiguationData":[OSD([sQuery(id+"F8.wireOp",EDGE,"E7.1.0")])],"isStart":false})]}),makeQuery(id+"F17.opExtrude","CAP_FACE",FACE,{"disambiguationData":[OSD([sQuery(id+"F10.wireOp",EDGE,"E11.62.0")])],"isStart":false})]}),makeQuery(id+"F18.opExtrude","CAP_FACE",FACE,{"disambiguationData":[OSD([sQuery(id+"F9.wireOp",EDGE,"E9.62.0")])],"isStart":false})]}),makeQuery(id+"F19.opExtrude","CAP_FACE",FACE,{"disambiguationData":[OSD([sQuery(id+"F8.wireOp",EDGE,"E7.62.0")])],"isStart":false})]})});
            var sketch = newSketch(context, id + "F26", { "sketchPlane" : qUnion([Q0])});
            skPoint(sketch, "E27.orphan", {"position": v(38.78, -46.21) * mm});
            skPoint(sketch, "E28.start.orphan", {"position": v(33.98, -49.84) * mm});
            skPoint(sketch, "E29.endSnap0", {"position": v(35.9, -47.4) * mm});
            skLineSegment(sketch, "E30", {"start": v(35.93, -46.38) * mm, "end": v(45.51, -59.03) * mm});
            skLineSegment(sketch, "E31", {"start": v(45.51, -59.03) * mm, "end": v(44.5, -59.8) * mm});
            skLineSegment(sketch, "E32", {"start": v(44.5, -59.8) * mm, "end": v(34.91, -47.15) * mm});
            skPoint(sketch, "E33.orphan", {"position": v(34.59, -47.4) * mm});
            skPoint(sketch, "E34.start.orphan", {"position": v(36.38, -48.03) * mm});
            skLineSegment(sketch, "E35", {"start": v(34.91, -47.15) * mm, "end": v(35.93, -46.38) * mm});
            skLineSegment(sketch, "E36.1.0", {"start": v(53.73, -23.55) * mm, "end": v(68.2, -30.08) * mm});
            skLineSegment(sketch, "E36.2.0", {"start": v(58.45, 5.01) * mm, "end": v(74.28, 6.2) * mm});
            skLineSegment(sketch, "E36.3.0", {"start": v(48.94, 32.36) * mm, "end": v(62.27, 40.97) * mm});
            skLineSegment(sketch, "E36.4.0", {"start": v(27.5, 51.82) * mm, "end": v(35.1, 65.76) * mm});
            skLineSegment(sketch, "E36.5.0", {"start": v(-0.63, 58.66) * mm, "end": v(-0.63, 74.54) * mm});
            skLineSegment(sketch, "E36.6.0", {"start": v(-28.6, 51.22) * mm, "end": v(-36.2, 65.16) * mm});
            skLineSegment(sketch, "E36.7.0", {"start": v(-49.62, 31.3) * mm, "end": v(-62.95, 39.92) * mm});
            skLineSegment(sketch, "E36.8.0", {"start": v(-58.55, 3.76) * mm, "end": v(-74.38, 4.95) * mm});
            skLineSegment(sketch, "E36.9.0", {"start": v(-53.22, -24.7) * mm, "end": v(-67.69, -31.22) * mm});
            skLineSegment(sketch, "E36.10.0", {"start": v(-34.93, -47.14) * mm, "end": v(-44.51, -59.79) * mm});
            skPoint(sketch, "E36.center", {"position": v(0, 0) * mm});
            skLineSegment(sketch, "E36.anchor1", {"start": v(0, 0) * mm, "end": v(45.51, -59.03) * mm, "construction": true});
            skLineSegment(sketch, "E36.anchor2", {"start": v(0, 0) * mm, "end": v(-44.51, -59.79) * mm, "construction": true});
            skLineSegment(sketch, "E37.1.0", {"start": v(67.68, -31.24) * mm, "end": v(53.2, -24.7) * mm});
            skLineSegment(sketch, "E37.2.0", {"start": v(74.38, 4.93) * mm, "end": v(58.55, 3.75) * mm});
            skLineSegment(sketch, "E37.3.0", {"start": v(62.96, 39.9) * mm, "end": v(49.62, 31.29) * mm});
            skLineSegment(sketch, "E37.4.0", {"start": v(36.21, 65.15) * mm, "end": v(28.62, 51.21) * mm});
            skLineSegment(sketch, "E37.5.0", {"start": v(0.64, 74.54) * mm, "end": v(0.64, 58.66) * mm});
            skLineSegment(sketch, "E37.6.0", {"start": v(-35.08, 65.77) * mm, "end": v(-27.5, 51.83) * mm});
            skLineSegment(sketch, "E37.7.0", {"start": v(-62.26, 40.98) * mm, "end": v(-48.93, 32.37) * mm});
            skLineSegment(sketch, "E37.8.0", {"start": v(-74.28, 6.22) * mm, "end": v(-58.45, 5.03) * mm});
            skLineSegment(sketch, "E37.9.0", {"start": v(-68.2, -30.06) * mm, "end": v(-53.74, -23.54) * mm});
            skLineSegment(sketch, "E37.10.0", {"start": v(-45.53, -59.02) * mm, "end": v(-35.94, -46.37) * mm});
            skLineSegment(sketch, "E37.anchor1", {"start": v(0, 0) * mm, "end": v(44.5, -59.8) * mm, "construction": true});
            skLineSegment(sketch, "E37.anchor2", {"start": v(0, 0) * mm, "end": v(-45.53, -59.02) * mm, "construction": true});
            skLineSegment(sketch, "E38.1.0", {"start": v(68.2, -30.08) * mm, "end": v(67.68, -31.24) * mm});
            skLineSegment(sketch, "E38.2.0", {"start": v(74.28, 6.2) * mm, "end": v(74.38, 4.93) * mm});
            skLineSegment(sketch, "E38.3.0", {"start": v(62.27, 40.97) * mm, "end": v(62.96, 39.9) * mm});
            skLineSegment(sketch, "E38.4.0", {"start": v(35.1, 65.76) * mm, "end": v(36.21, 65.15) * mm});
            skLineSegment(sketch, "E38.5.0", {"start": v(-0.63, 74.54) * mm, "end": v(0.64, 74.54) * mm});
            skLineSegment(sketch, "E38.6.0", {"start": v(-36.2, 65.16) * mm, "end": v(-35.08, 65.77) * mm});
            skLineSegment(sketch, "E38.7.0", {"start": v(-62.95, 39.92) * mm, "end": v(-62.26, 40.98) * mm});
            skLineSegment(sketch, "E38.8.0", {"start": v(-74.38, 4.95) * mm, "end": v(-74.28, 6.22) * mm});
            skLineSegment(sketch, "E38.9.0", {"start": v(-67.69, -31.22) * mm, "end": v(-68.2, -30.06) * mm});
            skLineSegment(sketch, "E38.10.0", {"start": v(-44.51, -59.79) * mm, "end": v(-45.53, -59.02) * mm});
            skLineSegment(sketch, "E39.1.0", {"start": v(53.2, -24.7) * mm, "end": v(53.73, -23.55) * mm});
            skLineSegment(sketch, "E39.2.0", {"start": v(58.55, 3.75) * mm, "end": v(58.45, 5.01) * mm});
            skLineSegment(sketch, "E39.3.0", {"start": v(49.62, 31.29) * mm, "end": v(48.94, 32.36) * mm});
            skLineSegment(sketch, "E39.4.0", {"start": v(28.62, 51.21) * mm, "end": v(27.5, 51.82) * mm});
            skLineSegment(sketch, "E39.5.0", {"start": v(0.64, 58.66) * mm, "end": v(-0.63, 58.66) * mm});
            skLineSegment(sketch, "E39.6.0", {"start": v(-27.5, 51.83) * mm, "end": v(-28.6, 51.22) * mm});
            skLineSegment(sketch, "E39.7.0", {"start": v(-48.93, 32.37) * mm, "end": v(-49.62, 31.3) * mm});
            skLineSegment(sketch, "E39.8.0", {"start": v(-58.45, 5.03) * mm, "end": v(-58.55, 3.76) * mm});
            skLineSegment(sketch, "E39.9.0", {"start": v(-53.74, -23.54) * mm, "end": v(-53.22, -24.7) * mm});
            skLineSegment(sketch, "E39.10.0", {"start": v(-35.94, -46.37) * mm, "end": v(-34.93, -47.14) * mm});
            skLineSegment(sketch, "E39.anchor1", {"start": v(0, 0) * mm, "end": v(34.91, -47.15) * mm, "construction": true});
            skLineSegment(sketch, "E39.anchor2", {"start": v(0, 0) * mm, "end": v(-35.94, -46.37) * mm, "construction": true});
            skSolve(sketch);
        }
        {
            var Q0;
            Q0 = qSketchRegion(id + "F26", true);
            extrude(context, id + "F27", {"entities" : qUnion([Q0]), "operationType" : NewBodyOperationType.REMOVE, "oppositeDirection" : true, "depth" : 1.59 * mm});
        }
        {
            var Q0;
            Q0=makeQuery(id+"F21.boolean.opBoolean","SPLIT",FACE,{"disambiguationData":[TD([makeQuery(id+"F13.boolean.opBoolean","COPY",FACE,{"derivedFrom":makeQuery(id+"F13.opExtrude","SWEPT_FACE",FACE,{"disambiguationData":[OSD([sQuery(id+"F10.wireOp",EDGE,"E10")])]})})])],"derivedFrom":makeQuery(id+"F19.boolean.opBoolean","MERGE",FACE,{"derivedFrom":[makeQuery(id+"F18.boolean.opBoolean","MERGE",FACE,{"derivedFrom":[makeQuery(id+"F17.boolean.opBoolean","MERGE",FACE,{"derivedFrom":[makeQuery(id+"F16.boolean.opBoolean","MERGE",FACE,{"derivedFrom":[makeQuery(id+"F15.boolean.opBoolean","MERGE",FACE,{"derivedFrom":[makeQuery(id+"F14.boolean.opBoolean","MERGE",FACE,{"derivedFrom":[makeQuery(id+"F7.opExtrude","CAP_FACE",FACE,{"disambiguationData":[OSD([sQuery(id+"F6.wireOp",EDGE,"E5")])],"isStart":false}),makeQuery(id+"F14.opExtrude","CAP_FACE",FACE,{"disambiguationData":[OSD([sQuery(id+"F10.wireOp",EDGE,"E11.1.0")])],"isStart":false})]}),makeQuery(id+"F15.opExtrude","CAP_FACE",FACE,{"disambiguationData":[OSD([sQuery(id+"F9.wireOp",EDGE,"E9.1.0")])],"isStart":false})]}),makeQuery(id+"F16.opExtrude","CAP_FACE",FACE,{"disambiguationData":[OSD([sQuery(id+"F8.wireOp",EDGE,"E7.1.0")])],"isStart":false})]}),makeQuery(id+"F17.opExtrude","CAP_FACE",FACE,{"disambiguationData":[OSD([sQuery(id+"F10.wireOp",EDGE,"E11.62.0")])],"isStart":false})]}),makeQuery(id+"F18.opExtrude","CAP_FACE",FACE,{"disambiguationData":[OSD([sQuery(id+"F9.wireOp",EDGE,"E9.62.0")])],"isStart":false})]}),makeQuery(id+"F19.opExtrude","CAP_FACE",FACE,{"disambiguationData":[OSD([sQuery(id+"F8.wireOp",EDGE,"E7.62.0")])],"isStart":false})]})});
            var sketch = newSketch(context, id + "F28", { "sketchPlane" : qUnion([Q0])});
            skCircle(sketch, "E40", {"center": v(0, 0) * mm, "radius": 54.84 * mm});
            skArc(sketch, "E41", {"start": v(-34.47, -34.47) * mm, "mid": v(48.75, 0) * mm, "end": v(-34.47, 34.47) * mm});
            skPoint(sketch, "E42.start.orphan", {"position": v(36.56, 0) * mm});
            skArc(sketch, "E43", {"start": v(-21.54, -21.54) * mm, "mid": v(30.47, 0) * mm, "end": v(-21.54, 21.54) * mm});
            skLineSegment(sketch, "E44", {"start": v(-21.54, -21.54) * mm, "end": v(-34.47, -34.47) * mm});
            skLineSegment(sketch, "E45", {"start": v(-21.54, 21.54) * mm, "end": v(-34.47, 34.47) * mm});
            skLineSegment(sketch, "E46", {"start": v(22.9, 0) * mm, "end": v(22.9, -15.84) * mm});
            skLineSegment(sketch, "E47", {"start": v(3.85, 0) * mm, "end": v(3.85, -15.84) * mm});
            skLineSegment(sketch, "E48", {"start": v(22.9, -15.84) * mm, "end": v(15.27, -15.84) * mm});
            skLineSegment(sketch, "E49", {"start": v(3.85, -15.84) * mm, "end": v(11.47, -15.84) * mm});
            skLineSegment(sketch, "E50", {"start": v(15.27, -15.84) * mm, "end": v(15.27, 0) * mm});
            skLineSegment(sketch, "E51", {"start": v(11.47, -15.84) * mm, "end": v(11.47, 0) * mm});
            skLineSegment(sketch, "E52", {"start": v(22.9, 0) * mm, "end": v(22.9, 12.03) * mm});
            skLineSegment(sketch, "E53", {"start": v(3.85, 0) * mm, "end": v(3.85, 12.03) * mm});
            skLineSegment(sketch, "E54.trimOffspring", {"start": v(15.27, -15.84) * mm, "end": v(22.9, -15.84) * mm});
            skLineSegment(sketch, "E55.trimOffspring", {"start": v(7.66, 15.84) * mm, "end": v(19.09, 15.84) * mm});
            skPoint(sketch, "E56.visualSharp", {"position": v(3.85, 15.84) * mm});
            skLineSegment(sketch, "E57", {"start": v(15.27, 0) * mm, "end": v(15.27, 7.93) * mm});
            skLineSegment(sketch, "E58", {"start": v(-27.88, -0.01) * mm, "end": v(-27.88, -12.03) * mm});
            skLineSegment(sketch, "E59", {"start": v(-27.88, 6.03) * mm, "end": v(-27.88, 12.03) * mm});
            skPoint(sketch, "E60.visualSharp", {"position": v(-21.54, 0) * mm});
            skLineSegment(sketch, "E61", {"start": v(-31.7, -15.84) * mm, "end": v(-43.12, -15.84) * mm});
            skLineSegment(sketch, "E62", {"start": v(-31.7, 15.84) * mm, "end": v(-43.12, 15.84) * mm});
            skLineSegment(sketch, "E63", {"start": v(-46.93, -0.01) * mm, "end": v(-46.93, 12.03) * mm});
            skLineSegment(sketch, "E64", {"start": v(-46.93, -0.01) * mm, "end": v(-46.93, -0.35) * mm});
            skPoint(sketch, "E65.visualSharp", {"position": v(-46.93, -15.84) * mm});
            skPoint(sketch, "E66.visualSharp", {"position": v(-27.88, -15.84) * mm});
            skPoint(sketch, "E67.visualSharp", {"position": v(-27.88, 15.84) * mm});
            skPoint(sketch, "E68.visualSharp", {"position": v(-46.93, 15.84) * mm});
            skLineSegment(sketch, "E69", {"start": v(11.47, 0) * mm, "end": v(11.47, 7.93) * mm});
            skArc(sketch, "E70", {"start": v(15.27, 7.93) * mm, "mid": v(13.37, 9.83) * mm, "end": v(11.47, 7.93) * mm});
            skArc(sketch, "E71.filletArc", {"start": v(22.9, 12.03) * mm, "mid": v(21.78, 14.73) * mm, "end": v(19.09, 15.84) * mm});
            skArc(sketch, "E72.filletArc", {"start": v(7.66, 15.84) * mm, "mid": v(4.97, 14.73) * mm, "end": v(3.85, 12.03) * mm});
            skLineSegment(sketch, "E73", {"start": v(-10.12, 9.83) * mm, "end": v(-10.12, 5.4) * mm});
            skLineSegment(sketch, "E74", {"start": v(-10.12, 5.4) * mm, "end": v(-13.3, 5.4) * mm});
            skLineSegment(sketch, "E75", {"start": v(-14.57, 6.66) * mm, "end": v(-14.57, 8.56) * mm});
            skLineSegment(sketch, "E76.trimOffspring", {"start": v(-10.12, 9.83) * mm, "end": v(-13.3, 9.83) * mm});
            skPoint(sketch, "E77.start.orphan", {"position": v(13.37, 9.83) * mm});
            skLineSegment(sketch, "E78", {"start": v(-10.12, -5.39) * mm, "end": v(-13.3, -5.39) * mm});
            skLineSegment(sketch, "E79", {"start": v(-14.56, -6.66) * mm, "end": v(-14.56, -8.56) * mm});
            skLineSegment(sketch, "E80", {"start": v(-13.3, -9.83) * mm, "end": v(-10.12, -9.83) * mm});
            skLineSegment(sketch, "E81", {"start": v(-10.12, -9.83) * mm, "end": v(-10.12, -5.39) * mm});
            skPoint(sketch, "E82.visualSharp", {"position": v(-14.56, -9.83) * mm});
            skArc(sketch, "E82.filletArc", {"start": v(-14.56, -8.56) * mm, "mid": v(-14.2, -9.46) * mm, "end": v(-13.3, -9.83) * mm});
            skPoint(sketch, "E83.visualSharp", {"position": v(-14.56, -5.39) * mm});
            skArc(sketch, "E83.filletArc", {"start": v(-13.3, -5.39) * mm, "mid": v(-14.2, -5.76) * mm, "end": v(-14.56, -6.66) * mm});
            skPoint(sketch, "E84.visualSharp", {"position": v(-14.57, 5.4) * mm});
            skArc(sketch, "E84.filletArc", {"start": v(-14.57, 6.66) * mm, "mid": v(-14.2, 5.76) * mm, "end": v(-13.3, 5.4) * mm});
            skPoint(sketch, "E85.visualSharp", {"position": v(-14.57, 9.83) * mm});
            skArc(sketch, "E85.filletArc", {"start": v(-13.3, 9.83) * mm, "mid": v(-14.2, 9.46) * mm, "end": v(-14.57, 8.56) * mm});
            skArc(sketch, "E86.filletArc", {"start": v(-31.7, -15.84) * mm, "mid": v(-29, -14.72) * mm, "end": v(-27.88, -12.03) * mm});
            skArc(sketch, "E87.filletArc", {"start": v(-46.93, -12.03) * mm, "mid": v(-45.81, -14.72) * mm, "end": v(-43.12, -15.84) * mm});
            skArc(sketch, "E88.filletArc", {"start": v(-43.12, 15.84) * mm, "mid": v(-45.81, 14.73) * mm, "end": v(-46.93, 12.03) * mm});
            skArc(sketch, "E89.filletArc", {"start": v(-27.88, 12.03) * mm, "mid": v(-29, 14.73) * mm, "end": v(-31.7, 15.84) * mm});
            skLineSegment(sketch, "E90", {"start": v(-39.3, 6.03) * mm, "end": v(-39.3, 8.12) * mm});
            skLineSegment(sketch, "E91", {"start": v(-35.49, 6.03) * mm, "end": v(-35.49, 8.12) * mm});
            skLineSegment(sketch, "E92", {"start": v(-27.88, 6.03) * mm, "end": v(-35.49, 6.03) * mm});
            skPoint(sketch, "E93.endSnap0", {"position": v(-37.4, 9.83) * mm});
            skArc(sketch, "E94", {"start": v(-35.49, 7.72) * mm, "mid": v(-37.4, 9.83) * mm, "end": v(-39.3, 7.72) * mm});
            skPoint(sketch, "E95.orphan", {"position": v(-39.3, 9.83) * mm});
            skPoint(sketch, "E93.start.orphan", {"position": v(-37.4, 9.83) * mm});
            skPoint(sketch, "E96.start.orphan", {"position": v(-35.49, 9.83) * mm});
            skPoint(sketch, "E97.orphan", {"position": v(-13.3, 6.03) * mm});
            skArc(sketch, "E98", {"start": v(-39.3, 6.03) * mm, "mid": v(-38.73, 4.67) * mm, "end": v(-37.36, 4.12) * mm});
            skLineSegment(sketch, "E99", {"start": v(-37.36, 4.12) * mm, "end": v(-31.7, 4.12) * mm});
            skLineSegment(sketch, "E100", {"start": v(-27.88, -0.01) * mm, "end": v(-27.88, 0.31) * mm});
            skPoint(sketch, "E101.visualSharp", {"position": v(-27.88, 4.12) * mm});
            skArc(sketch, "E101.filletArc", {"start": v(-27.88, 0.31) * mm, "mid": v(-29, 3) * mm, "end": v(-31.7, 4.12) * mm});
            skLineSegment(sketch, "E102", {"start": v(-46.93, -12.03) * mm, "end": v(-46.93, -6.02) * mm});
            skLineSegment(sketch, "E103", {"start": v(-46.93, -6.02) * mm, "end": v(-39.3, -6.02) * mm});
            skLineSegment(sketch, "E104", {"start": v(-39.3, -6.02) * mm, "end": v(-39.3, -8.1) * mm});
            skLineSegment(sketch, "E105", {"start": v(-35.49, -6.02) * mm, "end": v(-35.49, -8.1) * mm});
            skArc(sketch, "E106", {"start": v(-39.3, -8.1) * mm, "mid": v(-37.4, -10) * mm, "end": v(-35.49, -8.1) * mm});
            skLineSegment(sketch, "E107", {"start": v(-46.93, 12.03) * mm, "end": v(-46.93, -0.35) * mm});
            skLineSegment(sketch, "E108", {"start": v(-43.12, -4.16) * mm, "end": v(-36.99, -4.16) * mm});
            skPoint(sketch, "E109.visualSharp", {"position": v(-46.93, -4.16) * mm});
            skArc(sketch, "E109.filletArc", {"start": v(-46.93, -0.35) * mm, "mid": v(-45.81, -3.04) * mm, "end": v(-43.12, -4.16) * mm});
            skLineSegment(sketch, "E110.trimOffspring", {"start": v(-46.93, -6.02) * mm, "end": v(-46.93, -12.03) * mm});
            skArc(sketch, "E111", {"start": v(-35.49, -6.02) * mm, "mid": v(-35.9, -4.83) * mm, "end": v(-36.99, -4.16) * mm});
            skLineSegment(sketch, "E112", {"start": v(-2.5, -15.84) * mm, "end": v(-2.5, 15.84) * mm});
            skLineSegment(sketch, "E113", {"start": v(-2.5, -15.84) * mm, "end": v(-17.73, -15.84) * mm});
            skLineSegment(sketch, "E114", {"start": v(-2.5, 15.84) * mm, "end": v(-17.73, 15.84) * mm});
            skLineSegment(sketch, "E115", {"start": v(-21.54, -1.9) * mm, "end": v(-21.54, -12.03) * mm});
            skPoint(sketch, "E116.visualSharp", {"position": v(-21.54, -15.84) * mm});
            skArc(sketch, "E116.filletArc", {"start": v(-21.54, -12.03) * mm, "mid": v(-20.43, -14.72) * mm, "end": v(-17.73, -15.84) * mm});
            skPoint(sketch, "E117.visualSharp", {"position": v(-21.54, 15.84) * mm});
            skArc(sketch, "E117.filletArc", {"start": v(-17.73, 15.84) * mm, "mid": v(-20.43, 14.73) * mm, "end": v(-21.54, 12.03) * mm});
            skArc(sketch, "E118.filletArc", {"start": v(-19.64, 0) * mm, "mid": v(-20.99, -0.56) * mm, "end": v(-21.54, -1.9) * mm});
            skLineSegment(sketch, "E119", {"start": v(-21.54, 12.03) * mm, "end": v(-21.54, 1.9) * mm});
            skArc(sketch, "E120.filletArc", {"start": v(-21.54, 1.9) * mm, "mid": v(-20.99, 0.56) * mm, "end": v(-19.64, 0) * mm});
            skPoint(sketch, "E121.start.orphan", {"position": v(-2.5, 0) * mm});
            skSolve(sketch);
        }
        {
            var Q0;
            Q0=makeQuery(id+"F28.imprint","IMPRINT",FACE,{"disambiguationData":[TD([[makeQuery(id+"F28.imprint","IMPRINT",EDGE,{"derivedFrom":sQuery(id+"F28.wireOp",EDGE,"E40")}),1.0]])]});
            extrude(context, id + "F29", {"entities" : qUnion([Q0]), "operationType" : NewBodyOperationType.REMOVE, "oppositeDirection" : true, "depth" : 3.17 * mm});
        }
        {
            var Q0;
            Q0=makeQuery(id+"F29.boolean.opBoolean","SPLIT",FACE,{"disambiguationData":[TD([makeQuery(id+"F29.opExtrude","SWEPT_FACE",FACE,{"disambiguationData":[OSD([sQuery(id+"F28.wireOp",EDGE,"E112")])]})])],"derivedFrom":makeQuery(id+"F21.boolean.opBoolean","SPLIT",FACE,{"disambiguationData":[TD([makeQuery(id+"F13.boolean.opBoolean","COPY",FACE,{"derivedFrom":makeQuery(id+"F13.opExtrude","SWEPT_FACE",FACE,{"disambiguationData":[OSD([sQuery(id+"F10.wireOp",EDGE,"E10")])]})})])],"derivedFrom":makeQuery(id+"F19.boolean.opBoolean","MERGE",FACE,{"derivedFrom":[makeQuery(id+"F18.boolean.opBoolean","MERGE",FACE,{"derivedFrom":[makeQuery(id+"F17.boolean.opBoolean","MERGE",FACE,{"derivedFrom":[makeQuery(id+"F16.boolean.opBoolean","MERGE",FACE,{"derivedFrom":[makeQuery(id+"F15.boolean.opBoolean","MERGE",FACE,{"derivedFrom":[makeQuery(id+"F14.boolean.opBoolean","MERGE",FACE,{"derivedFrom":[makeQuery(id+"F7.opExtrude","CAP_FACE",FACE,{"disambiguationData":[OSD([sQuery(id+"F6.wireOp",EDGE,"E5")])],"isStart":false}),makeQuery(id+"F14.opExtrude","CAP_FACE",FACE,{"disambiguationData":[OSD([sQuery(id+"F10.wireOp",EDGE,"E11.1.0")])],"isStart":false})]}),makeQuery(id+"F15.opExtrude","CAP_FACE",FACE,{"disambiguationData":[OSD([sQuery(id+"F9.wireOp",EDGE,"E9.1.0")])],"isStart":false})]}),makeQuery(id+"F16.opExtrude","CAP_FACE",FACE,{"disambiguationData":[OSD([sQuery(id+"F8.wireOp",EDGE,"E7.1.0")])],"isStart":false})]}),makeQuery(id+"F17.opExtrude","CAP_FACE",FACE,{"disambiguationData":[OSD([sQuery(id+"F10.wireOp",EDGE,"E11.62.0")])],"isStart":false})]}),makeQuery(id+"F18.opExtrude","CAP_FACE",FACE,{"disambiguationData":[OSD([sQuery(id+"F9.wireOp",EDGE,"E9.62.0")])],"isStart":false})]}),makeQuery(id+"F19.opExtrude","CAP_FACE",FACE,{"disambiguationData":[OSD([sQuery(id+"F8.wireOp",EDGE,"E7.62.0")])],"isStart":false})]})})});
            var sketch = newSketch(context, id + "F30", { "sketchPlane" : qUnion([Q0])});
            skLineSegment(sketch, "E122", {"start": v(-10.11, 9.82) * mm, "end": v(-10.11, 5.38) * mm});
            skLineSegment(sketch, "E123", {"start": v(-10.11, 5.38) * mm, "end": v(-13.29, 5.38) * mm});
            skLineSegment(sketch, "E124", {"start": v(-14.56, 6.65) * mm, "end": v(-14.56, 8.55) * mm});
            skLineSegment(sketch, "E125", {"start": v(-13.29, 9.82) * mm, "end": v(-10.11, 9.82) * mm});
            skPoint(sketch, "E126.visualSharp", {"position": v(-14.56, 5.38) * mm});
            skArc(sketch, "E126.filletArc", {"start": v(-14.56, 6.65) * mm, "mid": v(-14.19, 5.75) * mm, "end": v(-13.29, 5.38) * mm});
            skPoint(sketch, "E127.visualSharp", {"position": v(-14.56, 9.82) * mm});
            skArc(sketch, "E127.filletArc", {"start": v(-13.29, 9.82) * mm, "mid": v(-14.19, 9.45) * mm, "end": v(-14.56, 8.55) * mm});
            skSolve(sketch);
        }
        {
            var Q0;
            Q0=makeQuery(id+"F30.imprint","IMPRINT",FACE,{"disambiguationData":[TD([[makeQuery(id+"F30.imprint","IMPRINT",EDGE,{"derivedFrom":sQuery(id+"F30.wireOp",EDGE,"E122")}),-1.0]])]});
            extrude(context, id + "F31", {"entities" : qUnion([Q0]), "operationType" : NewBodyOperationType.REMOVE, "oppositeDirection" : true, "depth" : 3.17 * mm});
        }
        {
            var Q0;
            Q0=makeQuery(id+"F29.boolean.opBoolean","SPLIT",FACE,{"disambiguationData":[TD([makeQuery(id+"F29.opExtrude","SWEPT_FACE",FACE,{"disambiguationData":[OSD([sQuery(id+"F28.wireOp",EDGE,"E112")])]})])],"derivedFrom":makeQuery(id+"F21.boolean.opBoolean","SPLIT",FACE,{"disambiguationData":[TD([makeQuery(id+"F13.boolean.opBoolean","COPY",FACE,{"derivedFrom":makeQuery(id+"F13.opExtrude","SWEPT_FACE",FACE,{"disambiguationData":[OSD([sQuery(id+"F10.wireOp",EDGE,"E10")])]})})])],"derivedFrom":makeQuery(id+"F19.boolean.opBoolean","MERGE",FACE,{"derivedFrom":[makeQuery(id+"F18.boolean.opBoolean","MERGE",FACE,{"derivedFrom":[makeQuery(id+"F17.boolean.opBoolean","MERGE",FACE,{"derivedFrom":[makeQuery(id+"F16.boolean.opBoolean","MERGE",FACE,{"derivedFrom":[makeQuery(id+"F15.boolean.opBoolean","MERGE",FACE,{"derivedFrom":[makeQuery(id+"F14.boolean.opBoolean","MERGE",FACE,{"derivedFrom":[makeQuery(id+"F7.opExtrude","CAP_FACE",FACE,{"disambiguationData":[OSD([sQuery(id+"F6.wireOp",EDGE,"E5")])],"isStart":false}),makeQuery(id+"F14.opExtrude","CAP_FACE",FACE,{"disambiguationData":[OSD([sQuery(id+"F10.wireOp",EDGE,"E11.1.0")])],"isStart":false})]}),makeQuery(id+"F15.opExtrude","CAP_FACE",FACE,{"disambiguationData":[OSD([sQuery(id+"F9.wireOp",EDGE,"E9.1.0")])],"isStart":false})]}),makeQuery(id+"F16.opExtrude","CAP_FACE",FACE,{"disambiguationData":[OSD([sQuery(id+"F8.wireOp",EDGE,"E7.1.0")])],"isStart":false})]}),makeQuery(id+"F17.opExtrude","CAP_FACE",FACE,{"disambiguationData":[OSD([sQuery(id+"F10.wireOp",EDGE,"E11.62.0")])],"isStart":false})]}),makeQuery(id+"F18.opExtrude","CAP_FACE",FACE,{"disambiguationData":[OSD([sQuery(id+"F9.wireOp",EDGE,"E9.62.0")])],"isStart":false})]}),makeQuery(id+"F19.opExtrude","CAP_FACE",FACE,{"disambiguationData":[OSD([sQuery(id+"F8.wireOp",EDGE,"E7.62.0")])],"isStart":false})]})})});
            var sketch = newSketch(context, id + "F32", { "sketchPlane" : qUnion([Q0])});
            skLineSegment(sketch, "E128", {"start": v(-10.11, -9.82) * mm, "end": v(-13.29, -9.82) * mm});
            skLineSegment(sketch, "E129", {"start": v(-14.56, -8.55) * mm, "end": v(-14.56, -6.64) * mm});
            skLineSegment(sketch, "E130", {"start": v(-13.29, -5.37) * mm, "end": v(-10.11, -5.37) * mm});
            skLineSegment(sketch, "E131", {"start": v(-10.11, -5.37) * mm, "end": v(-10.11, -9.82) * mm});
            skPoint(sketch, "E132.visualSharp", {"position": v(-14.56, -9.82) * mm});
            skArc(sketch, "E132.filletArc", {"start": v(-14.56, -8.55) * mm, "mid": v(-14.19, -9.45) * mm, "end": v(-13.29, -9.82) * mm});
            skPoint(sketch, "E133.visualSharp", {"position": v(-14.56, -5.37) * mm});
            skArc(sketch, "E133.filletArc", {"start": v(-13.29, -5.37) * mm, "mid": v(-14.19, -5.75) * mm, "end": v(-14.56, -6.64) * mm});
            skSolve(sketch);
        }
        {
            var Q0;
            Q0=makeQuery(id+"F32.imprint","IMPRINT",FACE,{"disambiguationData":[TD([[makeQuery(id+"F32.imprint","IMPRINT",EDGE,{"derivedFrom":sQuery(id+"F32.wireOp",EDGE,"E128")}),-1.0]])]});
            extrude(context, id + "F33", {"entities" : qUnion([Q0]), "operationType" : NewBodyOperationType.REMOVE, "oppositeDirection" : true, "depth" : 3.17 * mm});
        }
    });
